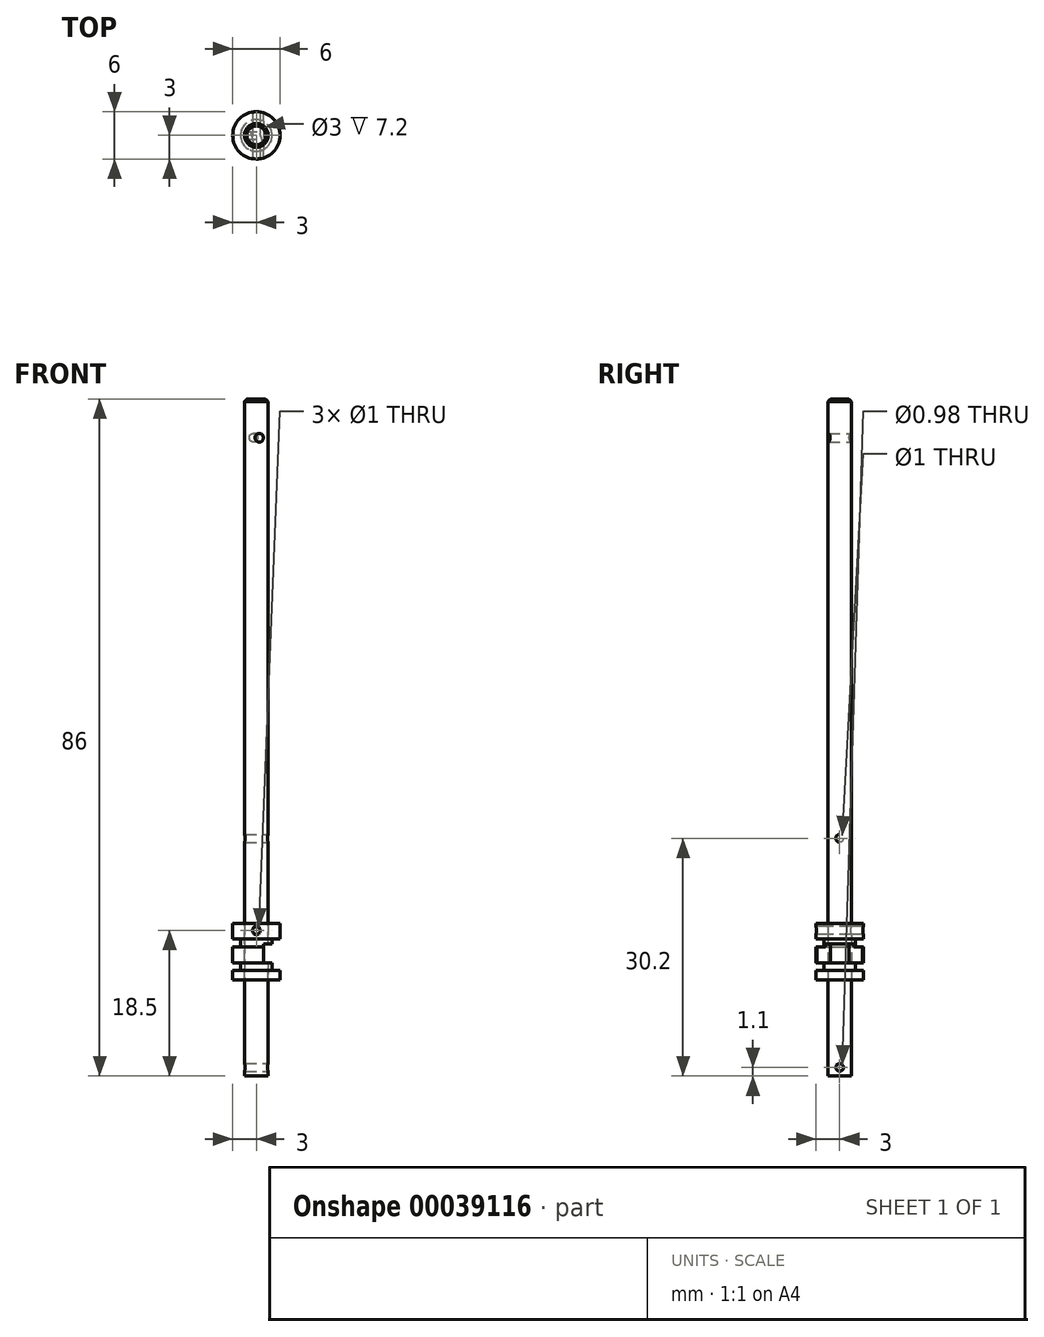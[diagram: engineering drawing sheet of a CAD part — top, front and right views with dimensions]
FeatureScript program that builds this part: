
annotation { "Feature Type Name" : "Feature", "Feature Type Description" : "" }
export const myFeature = defineFeature(function(context is Context, id is Id, definition is map)
    precondition{}
    {
        {
            var Q0;
            Q0=qCreatedBy(makeId("Front.planeOp"),FACE);
            var sketch = newSketch(context, id + "F0", { "sketchPlane" : qUnion([Q0])});
            skLineSegment(sketch, "E0.bottom", {"start": v(-1.5, 86) * mm, "end": v(0, 86) * mm});
            skLineSegment(sketch, "E0.top", {"start": v(-1.5, 0) * mm, "end": v(0, 0) * mm});
            skLineSegment(sketch, "E0.left", {"start": v(-1.5, 86) * mm, "end": v(-1.5, 0) * mm});
            skLineSegment(sketch, "E0.right", {"start": v(0, 86) * mm, "end": v(0, 0) * mm});
            skSolve(sketch);
        }
        {
            var Q0;
            Q0=makeQuery(id+"F0.imprint","IMPRINT",FACE,{"disambiguationData":[TD([[makeQuery(id+"F0.imprint","IMPRINT",EDGE,{"derivedFrom":sQuery(id+"F0.wireOp",EDGE,"E0.bottom")}),-1.0]])]});
            var Q1;
            Q1=sQuery(id+"F0.wireOp",EDGE,"E0.right");
            revolve(context, id + "F1", {"entities" : qUnion([Q0]), "axis" : qUnion([Q1]), "revolveType" : RevolveType.FULL});
        }
        {
            var Q0;
            Q0=makeQuery(id+"F1.opRevolve","SWEPT_EDGE",EDGE,{"disambiguationData":[OSD([sQuery(id+"F0.wireOp",EDGE,"E0.bottom"),sQuery(id+"F0.wireOp",EDGE,"E0.left")])]});
            chamfer(context, id + "F2", {"entities" : qUnion([Q0]), "chamferType" : ChamferType.OFFSET_ANGLE, "width" : 0.3 * mm, "oppositeDirection" : true, "angle" : 45 * degree, "tangentPropagation" : true});
        }
        {
            var Q0;
            Q0=qCreatedBy(makeId("Front.planeOp"),FACE);
            var Q1;
            Q1=makeQuery(id+"F1.opRevolve","SWEPT_FACE",FACE,{"disambiguationData":[OSD([sQuery(id+"F0.wireOp",EDGE,"E0.left")])]});
            cPlane(context, id + "F3", {"entities" : qUnion([Q0, Q1]), "cplaneType" : CPlaneType.LINE_ANGLE, "offset" : 150 * mm, "angle" : 15 * degree, "width" : 150 * mm, "height" : 150 * mm});
        }
        {
            var Q0;
            Q0=qCreatedBy(id+"F3.planeOp",FACE);
            var sketch = newSketch(context, id + "F4", { "sketchPlane" : qUnion([Q0])});
            skCircle(sketch, "E1", {"center": v(0, 81.1) * mm, "radius": 0.55 * mm});
            skSolve(sketch);
        }
        {
            var Q0;
            Q0=makeQuery(id+"F4.imprint","IMPRINT",FACE,{"disambiguationData":[TD([[makeQuery(id+"F4.imprint","IMPRINT",EDGE,{"derivedFrom":sQuery(id+"F4.wireOp",EDGE,"E1")}),1.0]])]});
            extrude(context, id + "F5", {"entities" : qUnion([Q0]), "operationType" : NewBodyOperationType.REMOVE, "endBound" : BoundingType.SYMMETRIC, "oppositeDirection" : true, "depth" : 8 * mm});
        }
        {
            var Q0;
            Q0=qCreatedBy(makeId("Front.planeOp"),FACE);
            var sketch = newSketch(context, id + "F6", { "sketchPlane" : qUnion([Q0])});
            skCircle(sketch, "E2", {"center": v(0, 18.5) * mm, "radius": 0.5 * mm});
            skSolve(sketch);
        }
        {
            var Q0;
            Q0=qCreatedBy(makeId("Right.planeOp"),FACE);
            var sketch = newSketch(context, id + "F7", { "sketchPlane" : qUnion([Q0])});
            skCircle(sketch, "E3", {"center": v(0, 1.1) * mm, "radius": 0.49 * mm});
            skSolve(sketch);
        }
        {
            var Q0;
            Q0=makeQuery(id+"F7.imprint","IMPRINT",FACE,{"disambiguationData":[TD([[makeQuery(id+"F7.imprint","IMPRINT",EDGE,{"derivedFrom":sQuery(id+"F7.wireOp",EDGE,"E3")}),1.0]])]});
            var Q1;
            Q1=sQuery(id+"F7.wireOp",EDGE,"E3");
            extrude(context, id + "F8", {"entities" : qUnion([Q0]), "operationType" : NewBodyOperationType.REMOVE, "surfaceEntities" : qUnion([Q1]), "endBound" : BoundingType.SYMMETRIC, "oppositeDirection" : true, "depth" : 4 * mm});
        }
        {
            var Q0;
            Q0=qCreatedBy(makeId("Front.planeOp"),FACE);
            var sketch = newSketch(context, id + "F9", { "sketchPlane" : qUnion([Q0])});
            skLineSegment(sketch, "E4", {"start": v(-1.5, 12.2) * mm, "end": v(-1.5, 19.4) * mm});
            skLineSegment(sketch, "E5", {"start": v(-1.5, 19.4) * mm, "end": v(-3, 19.4) * mm});
            skLineSegment(sketch, "E6", {"start": v(-3, 19.4) * mm, "end": v(-3, 17.4) * mm});
            skLineSegment(sketch, "E7", {"start": v(-3, 17.4) * mm, "end": v(-2, 17.4) * mm});
            skLineSegment(sketch, "E8", {"start": v(-2, 17.4) * mm, "end": v(-2, 16.4) * mm});
            skLineSegment(sketch, "E9", {"start": v(-2, 16.4) * mm, "end": v(-3, 16.4) * mm});
            skLineSegment(sketch, "E10", {"start": v(-3, 16.4) * mm, "end": v(-3, 14.4) * mm});
            skLineSegment(sketch, "E11", {"start": v(-3, 14.4) * mm, "end": v(-2, 14.4) * mm});
            skLineSegment(sketch, "E12", {"start": v(-2, 14.4) * mm, "end": v(-2, 13.4) * mm});
            skLineSegment(sketch, "E13", {"start": v(-2, 13.4) * mm, "end": v(-3, 13.4) * mm});
            skLineSegment(sketch, "E14", {"start": v(-3, 13.4) * mm, "end": v(-3, 12.2) * mm});
            skLineSegment(sketch, "E15", {"start": v(-3, 12.2) * mm, "end": v(-1.5, 12.2) * mm});
            skSolve(sketch);
        }
        {
            var Q0;
            Q0=makeQuery(id+"F9.imprint","IMPRINT",FACE,{"disambiguationData":[TD([[makeQuery(id+"F9.imprint","IMPRINT",EDGE,{"derivedFrom":sQuery(id+"F9.wireOp",EDGE,"E4")}),1.0]])]});
            var Q1;
            Q1=makeQuery(id+"F1.opRevolve","SWEPT_FACE",FACE,{"disambiguationData":[OSD([sQuery(id+"F0.wireOp",EDGE,"E0.left")])]});
            revolve(context, id + "F10", {"entities" : qUnion([Q0]), "axis" : qUnion([Q1]), "revolveType" : RevolveType.FULL});
        }
        {
            var Q0;
            Q0=qCreatedBy(makeId("Front.planeOp"),FACE);
            var sketch = newSketch(context, id + "F11", { "sketchPlane" : qUnion([Q0])});
            skLineSegment(sketch, "E16.bottom", {"start": v(0.9, 16.8) * mm, "end": v(3, 16.8) * mm});
            skLineSegment(sketch, "E16.top", {"start": v(0.9, 14.4) * mm, "end": v(3, 14.4) * mm});
            skLineSegment(sketch, "E16.left", {"start": v(0.9, 16.8) * mm, "end": v(0.9, 14.4) * mm});
            skLineSegment(sketch, "E16.right", {"start": v(3, 16.8) * mm, "end": v(3, 14.4) * mm});
            skLineSegment(sketch, "E17.0", {"start": v(3, 19.4) * mm, "end": v(-3, 19.4) * mm});
            skSolve(sketch);
        }
        {
            var Q0;
            Q0 = qSketchRegion(id + "F11", true);
            extrude(context, id + "F12", {"entities" : qUnion([Q0]), "operationType" : NewBodyOperationType.REMOVE, "endBound" : BoundingType.SYMMETRIC, "oppositeDirection" : true, "depth" : 6 * mm});
        }
        {
            var Q0;
            Q0=makeQuery(id+"F6.imprint","IMPRINT",FACE,{"disambiguationData":[TD([[makeQuery(id+"F6.imprint","IMPRINT",EDGE,{"derivedFrom":sQuery(id+"F6.wireOp",EDGE,"E2")}),1.0]])]});
            var Q1;
            Q1=sQuery(id+"F6.wireOp",EDGE,"E2");
            extrude(context, id + "F13", {"entities" : qUnion([Q0]), "operationType" : NewBodyOperationType.REMOVE, "surfaceEntities" : qUnion([Q1]), "endBound" : BoundingType.SYMMETRIC, "oppositeDirection" : true, "depth" : 6 * mm});
        }
        {
            var Q0;
            Q0=qCreatedBy(makeId("Right.planeOp"),FACE);
            var sketch = newSketch(context, id + "F14", { "sketchPlane" : qUnion([Q0])});
            skCircle(sketch, "E18", {"center": v(0, 30.2) * mm, "radius": 0.5 * mm});
            skSolve(sketch);
        }
        {
            var Q0;
            Q0 = qSketchRegion(id + "F14", true);
            extrude(context, id + "F15", {"entities" : qUnion([Q0]), "operationType" : NewBodyOperationType.REMOVE, "endBound" : BoundingType.SYMMETRIC, "oppositeDirection" : true, "depth" : 5 * mm});
        }
    });
